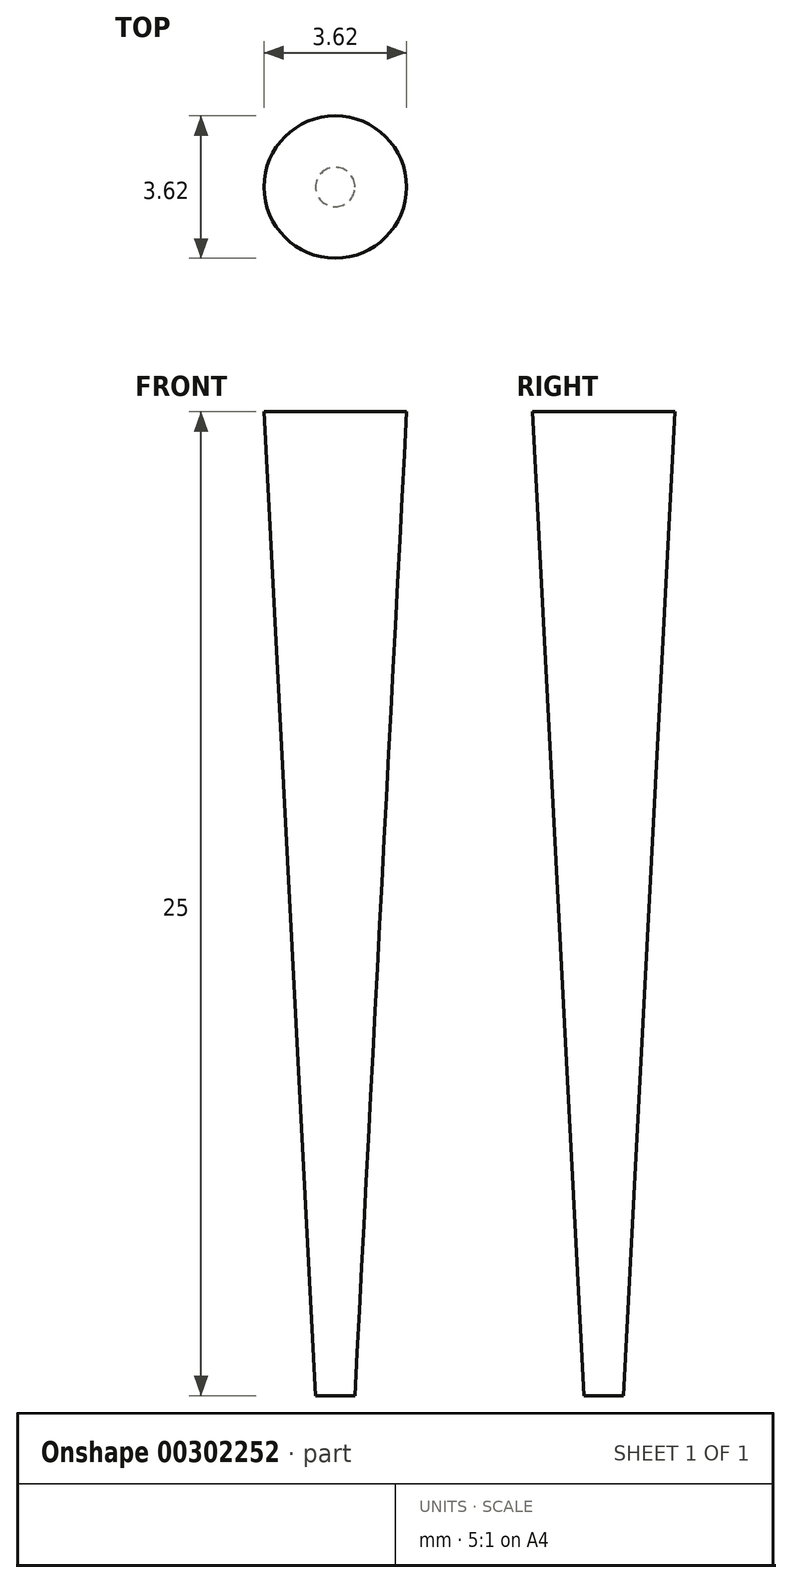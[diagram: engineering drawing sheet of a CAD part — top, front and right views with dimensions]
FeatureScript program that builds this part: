
annotation { "Feature Type Name" : "Feature", "Feature Type Description" : "" }
export const myFeature = defineFeature(function(context is Context, id is Id, definition is map)
    precondition{}
    {
        {
            var Q0;
            Q0=qCreatedBy(makeId("Top.planeOp"),FACE);
            var sketch = newSketch(context, id + "F0", { "sketchPlane" : qUnion([Q0])});
            skCircle(sketch, "E0", {"center": v(0, 0) * mm, "radius": 0.5 * mm});
            skSolve(sketch);
        }
        {
            var Q0;
            Q0 = qSketchRegion(id + "F0", true);
            extrude(context, id + "F1", {"entities" : qUnion([Q0]), "depth" : 25 * mm, "hasDraft" : true, "draftAngle" : 3 * degree});
        }
    });
